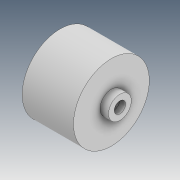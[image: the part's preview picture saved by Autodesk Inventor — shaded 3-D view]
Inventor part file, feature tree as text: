
AUTODESK INVENTOR PART (.ipt)
format: ipt  version: 2021 (Build 250183000, 183)  size: 116,224 bytes
history: native  units: in
note: dims shown in document units (in); Inventor stores cm internally (conversion verified against a paired STEP export)
features: sketch x6, extrude x3, other x2
ambient origin geometry x8: Origin, YZ Plane, XZ Plane, XY Plane, X Axis, Y Axis, Z Axis, Center Point
bodies: Body1 (feature_tree)
feature tree (11):
  other  "Sólido1"
  other  "Revolução1"
  extrude  "Extrusão1"  Depth=0.2618in
  extrude  "Extrusão2"  Depth=0.0984in
  sketch  "Esboço4"  dims[d6=0.0591in d7=0.0in]
  sketch  "Esboço5"  dims[d8=0.1181in]
  extrude  "Extrusão3"  Depth=0.1575in
  sketch  "Esboço1"  dims[d0=0.3543in d1=0.2618in]
  sketch  "Esboço2"  dims[d2=0.0787in d3=0.0984in]
  sketch  "Esboço3"  dims[d4=90.0deg d5=0.1575in]
  sketch  "Esboço6"  dims[d9=0.1575in d10=0.0in d11=0.0787in d12=0.0417in d13=0.0in]
